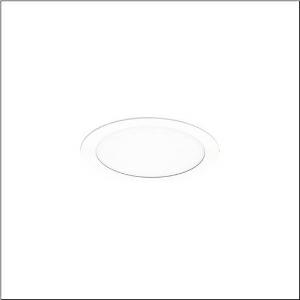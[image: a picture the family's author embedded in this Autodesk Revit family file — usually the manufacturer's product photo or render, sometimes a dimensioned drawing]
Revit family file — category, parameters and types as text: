
# Revit family: lunis_21_l_51db16md91c
name_source: partatom
category: Lighting Fixtures
units: mm (PartAtom-declared; Revit-internal decimal feet)

## family parameters
Cut with Voids When Loaded = No
Host = Face
Light Source = No
Part Type = Normal
Room Calculation Point = No
Round Connector Dimension = Use Diameter
Shared = No

## types (1)
- --- (1 x LED, 3020 lm, 21.7 W, 6500K)
    Apparent Load = 22 VA
    CIE Flux Codes = 50 80 96 100 100
    Color Rendering = 80
    Color Temperature = 6500K
    Default Elevation = 1800 mm
    Description = Lunis 21,  L, downlight, light control with lens, of PMMA, optical cover: cover panel, of PC, opal, light emission: direct distribution, LED rated luminous flux: 1.750lm, light colour: 830/840/865, with terminal, 3-pole, mains connection: 220..240V, AC/DC, 0/50..60Hz, housing, round, of diecast aluminium, traffic white (RAL 9016), diameter: 165mm, clamping range: 1..40mm, protection rating (complete): IP20, protection rating (on room side): IP54, insulation class (complete): insulation class II (safety insulation), certification: CE, impact resistance: IK03, packaging unit: 1 piece
    Height = 0 mm  [stored 0 ft]
    Lamp = 1 x LED
    Lamp Light Flux = 3020 lm
    Lamp Power = 21.7 W
    Lamp count = 1
    Length = 165 mm
    Luminous efficacy = 139 lm/W
    Manufacturer = Siteco
    ModVariant = No
    Model = 51DB16MD91C
    Mounting Place = Ceiling
    Mounting Type = Recessed
    Number of Poles = 1
    OnlyDefault = Yes
    Power Factor = 1
    Product Name = Lunis 21 L
    Product group = downlight
    ProductGroupID = 401
    Protection Class = Protection class II
    Protection Degree = IP 20
    RLX_Detail_Level = 1
    RLX_Emergency_Light_Flux = 0 lm
    RLX_Emergency_Type = 0
    RLX_Emergency_Type_DB = No
    RlxData = <blob elided: 13709 chars, md5=f9d81a84>
    Socket = socket
    Standby Power = 0 W
    System Light Flux = 3020 lm
    System Power = 22 W
    Type Comments = individual setting: colour temperature 6500K, luminous flux: 100 % | (OFF | ON | ON | ON) | 650 mA
    Type Image = l_1291165.jpg
    URL = http://relux.com
    VarID = @adj_017812
    Voltage = 0 V
    Weight = 0.00 kg
    Width = 0 mm  [stored 0 ft]

note: [stored X ft] marks values corroborated as IEEE doubles in the binary element streams (Revit-internal decimal feet)

## geometry (parser evidence)
native form markers: Sweep x11
no freeform markers — native parametric forms only
